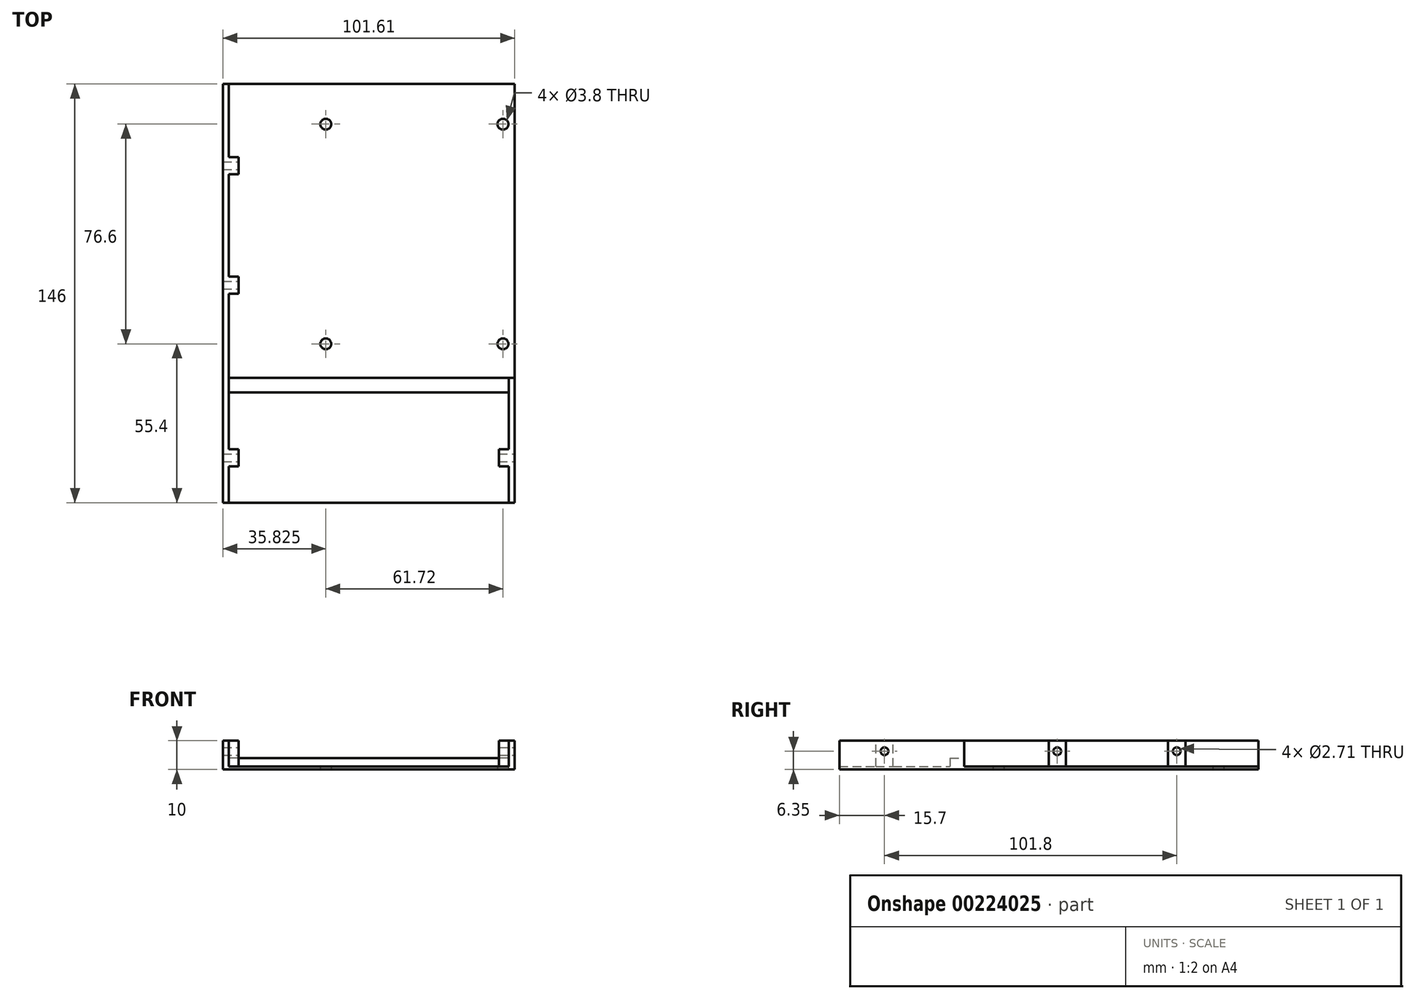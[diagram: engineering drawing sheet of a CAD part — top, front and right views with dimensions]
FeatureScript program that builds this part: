
annotation { "Feature Type Name" : "Feature", "Feature Type Description" : "" }
export const myFeature = defineFeature(function(context is Context, id is Id, definition is map)
    precondition{}
    {
        {
            var Q0;
            Q0=qCreatedBy(makeId("Top.planeOp"),FACE);
            var sketch = newSketch(context, id + "F0", { "sketchPlane" : qUnion([Q0])});
            skLineSegment(sketch, "E0.bottom", {"start": v(0, 0) * mm, "end": v(-101.61, 0) * mm});
            skLineSegment(sketch, "E0.top", {"start": v(0, -146) * mm, "end": v(-101.6, -146) * mm});
            skLineSegment(sketch, "E0.left", {"start": v(0, 0) * mm, "end": v(0, -146) * mm});
            skLineSegment(sketch, "E0.right", {"start": v(-101.61, 0) * mm, "end": v(-101.6, -146) * mm});
            skLineSegment(sketch, "E1", {"start": v(-50.8, 0) * mm, "end": v(-50.8, -146) * mm, "construction": true});
            skLineSegment(sketch, "E2", {"start": v(-98.43, 0) * mm, "end": v(-98.43, -146) * mm, "construction": true});
            skLineSegment(sketch, "E3.MirrorCS", {"start": v(-3.18, 0) * mm, "end": v(-3.18, -146) * mm, "construction": true});
            skPoint(sketch, "E4", {"position": v(-3.18, -41.28) * mm});
            skPoint(sketch, "E5", {"position": v(-3.18, -85.73) * mm});
            skPoint(sketch, "E6.MirrorP", {"position": v(-98.43, -85.73) * mm});
            skPoint(sketch, "E7.MirrorP", {"position": v(-98.43, -41.28) * mm});
            skSolve(sketch);
        }
        {
            var Q0;
            Q0=qSketchRegion(id+"F0",true);
            extrude(context, id + "F1", {"entities" : qUnion([Q0]), "oppositeDirection" : true, "depth" : 1 * mm});
        }
        {
            var Q0;
            Q0=qCreatedBy(makeId("Top.planeOp"),FACE);
            var sketch = newSketch(context, id + "F2", { "sketchPlane" : qUnion([Q0])});
            skLineSegment(sketch, "E8.bottom", {"start": v(0, 0) * mm, "end": v(-69.85, 0) * mm});
            skLineSegment(sketch, "E8.top", {"start": v(0, -100.5) * mm, "end": v(-69.85, -100.5) * mm});
            skLineSegment(sketch, "E8.left", {"start": v(0, 0) * mm, "end": v(0, -100.5) * mm});
            skLineSegment(sketch, "E8.right", {"start": v(-69.85, 0) * mm, "end": v(-69.85, -100.5) * mm});
            skLineSegment(sketch, "E9", {"start": v(-34.92, -100.5) * mm, "end": v(-34.92, 0) * mm, "construction": true});
            skLineSegment(sketch, "E10", {"start": v(-4.07, 0) * mm, "end": v(-4.06, -100.5) * mm, "construction": true});
            skLineSegment(sketch, "E11.MirrorCS", {"start": v(-65.78, 0) * mm, "end": v(-65.78, -100.5) * mm, "construction": true});
            skPoint(sketch, "E12", {"position": v(-4.07, -14) * mm});
            skPoint(sketch, "E13", {"position": v(-4.06, -90.6) * mm});
            skPoint(sketch, "E14", {"position": v(-65.78, -14) * mm});
            skPoint(sketch, "E15", {"position": v(-65.79, -90.6) * mm});
            skSolve(sketch);
        }
        {
            var Q0;
            Q0=qCreatedBy(makeId("Top.planeOp"),FACE);
            var sketch = newSketch(context, id + "F3", { "sketchPlane" : qUnion([Q0])});
            skLineSegment(sketch, "E16.bottom", {"start": v(-101.6, -146) * mm, "end": v(-99.6, -146) * mm});
            skLineSegment(sketch, "E16.top", {"start": v(-101.61, 0) * mm, "end": v(-99.61, 0) * mm});
            skLineSegment(sketch, "E16.left", {"start": v(-101.6, -146) * mm, "end": v(-101.6, 0) * mm});
            skLineSegment(sketch, "E16.right", {"start": v(-99.6, -146) * mm, "end": v(-99.6, 0) * mm});
            skLineSegment(sketch, "E17.bottom", {"start": v(0, -146) * mm, "end": v(-2, -146) * mm});
            skLineSegment(sketch, "E17.top", {"start": v(0, -102.5) * mm, "end": v(-2, -102.5) * mm});
            skLineSegment(sketch, "E17.left", {"start": v(0, -146) * mm, "end": v(0, -102.5) * mm});
            skLineSegment(sketch, "E17.right", {"start": v(-2, -146) * mm, "end": v(-2, -102.5) * mm});
            skSolve(sketch);
        }
        {
            var Q0;
            Q0=qSketchRegion(id+"F3",true);
            extrude(context, id + "F4", {"entities" : qUnion([Q0]), "operationType" : NewBodyOperationType.ADD, "depth" : 9 * mm});
        }
        {
            var Q0;
            Q0=makeQuery(id+"F1.opExtrude","CAP_FACE",FACE,{"disambiguationData":[OSD([sQuery(id+"F0.wireOp",EDGE,"E0.bottom"),sQuery(id+"F0.wireOp",EDGE,"E0.top"),sQuery(id+"F0.wireOp",EDGE,"E0.left"),sQuery(id+"F0.wireOp",EDGE,"E0.right")])],"isStart":true});
            var sketch = newSketch(context, id + "F5", { "sketchPlane" : qUnion([Q0])});
            skLineSegment(sketch, "E18.bottom", {"start": v(-2, -102.5) * mm, "end": v(-99.6, -102.5) * mm});
            skLineSegment(sketch, "E18.top", {"start": v(-2, -107.5) * mm, "end": v(-99.6, -107.5) * mm});
            skLineSegment(sketch, "E18.left", {"start": v(-2, -102.5) * mm, "end": v(-2, -107.5) * mm});
            skLineSegment(sketch, "E18.right", {"start": v(-99.6, -102.5) * mm, "end": v(-99.6, -107.5) * mm});
            skSolve(sketch);
        }
        {
            var Q0;
            Q0=qSketchRegion(id+"F5",true);
            extrude(context, id + "F6", {"entities" : qUnion([Q0]), "operationType" : NewBodyOperationType.ADD, "depth" : 3 * mm});
        }
        {
            var Q0;
            Q0=makeQuery(id+"F4.boolean.opBoolean","MERGE",FACE,{"derivedFrom":[makeQuery(id+"F1.opExtrude","SWEPT_FACE",FACE,{"disambiguationData":[OSD([sQuery(id+"F0.wireOp",EDGE,"E0.right")])]}),makeQuery(id+"F4.opExtrude","SWEPT_FACE",FACE,{"disambiguationData":[OSD([sQuery(id+"F3.wireOp",EDGE,"E16.left")])]})]});
            var sketch = newSketch(context, id + "F7", { "sketchPlane" : qUnion([Q0])});
            skPoint(sketch, "E19", {"position": v(28.5, 5.35) * mm});
            skPoint(sketch, "E20", {"position": v(70.1, 5.35) * mm});
            skPoint(sketch, "E21", {"position": v(130.3, 5.35) * mm});
            skLineSegment(sketch, "E22", {"start": v(0, 5.35) * mm, "end": v(146, 5.35) * mm, "construction": true});
            skSolve(sketch);
        }
        {
            var Q0;
            Q0=makeQuery(id+"F4.boolean.opBoolean","MERGE",FACE,{"derivedFrom":[makeQuery(id+"F1.opExtrude","SWEPT_FACE",FACE,{"disambiguationData":[OSD([sQuery(id+"F0.wireOp",EDGE,"E0.left")])]}),makeQuery(id+"F4.opExtrude","SWEPT_FACE",FACE,{"disambiguationData":[OSD([sQuery(id+"F3.wireOp",EDGE,"E17.left")])]})]});
            var sketch = newSketch(context, id + "F8", { "sketchPlane" : qUnion([Q0])});
            skPoint(sketch, "E23", {"position": v(-130.3, 5.35) * mm});
            skSolve(sketch);
        }
        {
            var Q0;
            Q0=makeQuery(id+"F1.opExtrude","CAP_FACE",FACE,{"disambiguationData":[OSD([sQuery(id+"F0.wireOp",EDGE,"E0.bottom"),sQuery(id+"F0.wireOp",EDGE,"E0.top"),sQuery(id+"F0.wireOp",EDGE,"E0.left"),sQuery(id+"F0.wireOp",EDGE,"E0.right")])],"isStart":true});
            var sketch = newSketch(context, id + "F9", { "sketchPlane" : qUnion([Q0])});
            skLineSegment(sketch, "E24.bottom", {"start": v(-96.1, -133.3) * mm, "end": v(-101.6, -133.3) * mm});
            skLineSegment(sketch, "E24.top", {"start": v(-96.1, -127.3) * mm, "end": v(-101.6, -127.3) * mm});
            skLineSegment(sketch, "E24.left", {"start": v(-96.1, -133.3) * mm, "end": v(-96.1, -127.3) * mm});
            skLineSegment(sketch, "E24.right", {"start": v(-101.6, -133.3) * mm, "end": v(-101.6, -127.3) * mm});
            skLineSegment(sketch, "E25.bottom", {"start": v(-101.6, -73.11) * mm, "end": v(-96.1, -73.11) * mm});
            skLineSegment(sketch, "E25.top", {"start": v(-101.6, -67.11) * mm, "end": v(-96.1, -67.11) * mm});
            skLineSegment(sketch, "E25.left", {"start": v(-101.6, -73.11) * mm, "end": v(-101.6, -67.11) * mm});
            skLineSegment(sketch, "E25.right", {"start": v(-96.1, -73.11) * mm, "end": v(-96.1, -67.11) * mm});
            skLineSegment(sketch, "E26.bottom", {"start": v(-101.61, -31.5) * mm, "end": v(-96.11, -31.5) * mm});
            skLineSegment(sketch, "E26.top", {"start": v(-101.61, -25.5) * mm, "end": v(-96.11, -25.5) * mm});
            skLineSegment(sketch, "E26.left", {"start": v(-101.61, -31.5) * mm, "end": v(-101.61, -25.5) * mm});
            skLineSegment(sketch, "E26.right", {"start": v(-96.11, -31.5) * mm, "end": v(-96.11, -25.5) * mm});
            skLineSegment(sketch, "E27.bottom", {"start": v(0, -133.3) * mm, "end": v(-5.5, -133.3) * mm});
            skLineSegment(sketch, "E27.top", {"start": v(0, -127.3) * mm, "end": v(-5.5, -127.3) * mm});
            skLineSegment(sketch, "E27.left", {"start": v(0, -133.3) * mm, "end": v(0, -127.3) * mm});
            skLineSegment(sketch, "E27.right", {"start": v(-5.5, -133.3) * mm, "end": v(-5.5, -127.3) * mm});
            skSolve(sketch);
        }
        {
            var Q0;
            Q0=qSketchRegion(id+"F9",true);
            var Q1;
            Q1=makeQuery(id+"F4.opExtrude","CAP_FACE",FACE,{"disambiguationData":[OSD([sQuery(id+"F3.wireOp",EDGE,"E16.bottom"),sQuery(id+"F3.wireOp",EDGE,"E16.top"),sQuery(id+"F3.wireOp",EDGE,"E16.left"),sQuery(id+"F3.wireOp",EDGE,"E16.right")])],"isStart":false});
            extrude(context, id + "F10", {"entities" : qUnion([Q0]), "operationType" : NewBodyOperationType.ADD, "endBound" : BoundingType.UP_TO_SURFACE, "endBoundEntityFace" : qUnion([Q1]), "depth" : 8.6 * mm});
        }
        {
            var Q0;
            Q0=sQuery(id+"F7.wireOp",VERTEX,"E19");
            var Q1;
            Q1=sQuery(id+"F7.wireOp",VERTEX,"E20");
            var Q2;
            Q2=sQuery(id+"F7.wireOp",VERTEX,"E21");
            var Q3;
            Q3=makeQuery(id+"F1.opExtrude","SWEPT_BODY",BODY,{"disambiguationData":[OSD([sQuery(id+"F0.wireOp",EDGE,"E0.bottom"),sQuery(id+"F0.wireOp",EDGE,"E0.top"),sQuery(id+"F0.wireOp",EDGE,"E0.left"),sQuery(id+"F0.wireOp",EDGE,"E0.right")])]});
            hole(context, id + "F11", {"style" : HoleStyle.SIMPLE, "endStyle" : HoleEndStyle.THROUGH, "standardTappedOrClearance" : lookupTablePath({ "standard" : "ANSI", "engagement" : "75%", "pitch" : "32 tpi", "size" : "#6", "type" : "Tapped" }), "standardBlindInLast" : lookupTablePath({ "standard" : "ANSI", "engagement" : "75%", "pitch" : "32 tpi", "size" : "#6", "type" : "Tapped" }), "holeDiameter" : 2.7 * mm, "showTappedDepth" : true, "tappedDepth" : 12 * mm, "tapClearance" : 3, "locations" : qUnion([Q0, Q1, Q2]), "scope" : qUnion([Q3]), "majorDiameter" : 3.5 * mm, "startStyle" : HoleStartStyle.SKETCH});
        }
        {
            var Q0;
            Q0=sQuery(id+"F2.wireOp",VERTEX,"E15");
            var Q1;
            Q1=sQuery(id+"F2.wireOp",VERTEX,"E13");
            var Q2;
            Q2=sQuery(id+"F2.wireOp",VERTEX,"E12");
            var Q3;
            Q3=sQuery(id+"F2.wireOp",VERTEX,"E14");
            var Q4;
            Q4=makeQuery(id+"F1.opExtrude","SWEPT_BODY",BODY,{"disambiguationData":[OSD([sQuery(id+"F0.wireOp",EDGE,"E0.bottom"),sQuery(id+"F0.wireOp",EDGE,"E0.top"),sQuery(id+"F0.wireOp",EDGE,"E0.left"),sQuery(id+"F0.wireOp",EDGE,"E0.right")])]});
            hole(context, id + "F12", {"style" : HoleStyle.SIMPLE, "endStyle" : HoleEndStyle.THROUGH, "standardTappedOrClearance" : lookupTablePath({ "standard" : "ANSI", "fit" : "Normal (ASME)", "size" : "#6", "type" : "Clearance" }), "standardBlindInLast" : lookupTablePath({ "fit" : "Free", "standard" : "ANSI", "size" : "#6", "type" : "Clearance" }), "holeDiameter" : 3.8 * mm, "tappedDepth" : 12 * mm, "tapClearance" : 3, "locations" : qUnion([Q0, Q1, Q2, Q3]), "scope" : qUnion([Q4]), "startStyle" : HoleStartStyle.SKETCH});
        }
    });
